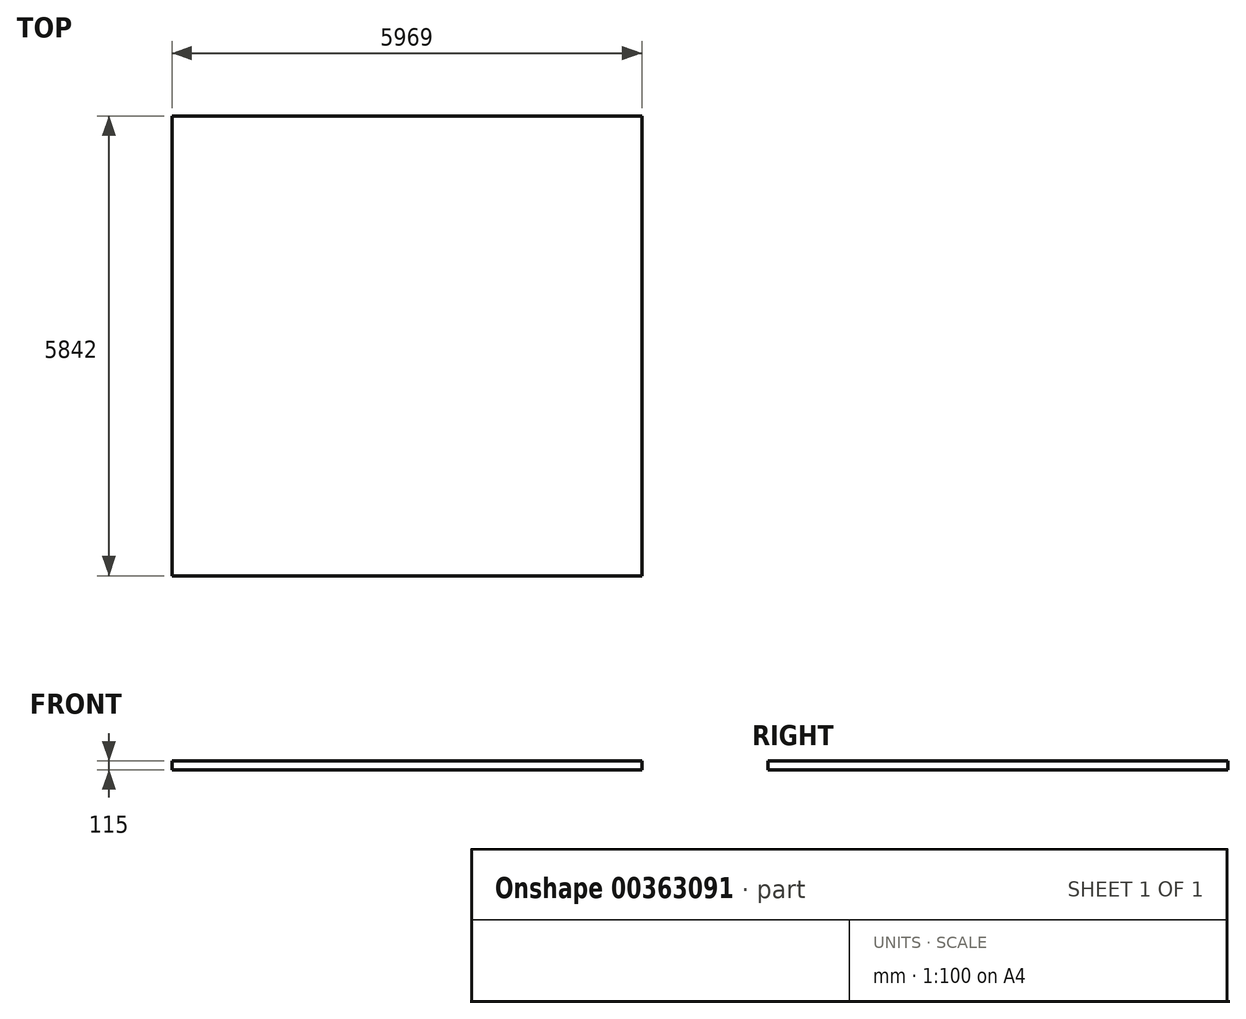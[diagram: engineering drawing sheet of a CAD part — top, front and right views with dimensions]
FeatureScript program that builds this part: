
annotation { "Feature Type Name" : "Feature", "Feature Type Description" : "" }
export const myFeature = defineFeature(function(context is Context, id is Id, definition is map)
    precondition{}
    {
        {
            assignVariable(context, id + "F0", {"name" : "hgt", "anyValue" : 115});
        }
        {
            var Q0;
            Q0=qCreatedBy(makeId("Top.planeOp"),FACE);
            var sketch = newSketch(context, id + "F1", { "sketchPlane" : qUnion([Q0])});
            skLineSegment(sketch, "E0.bottom", {"start": v(2984.5, 2921) * mm, "end": v(-2984.5, 2921) * mm});
            skLineSegment(sketch, "E0.top", {"start": v(2984.5, -2921) * mm, "end": v(-2984.5, -2921) * mm});
            skLineSegment(sketch, "E0.left", {"start": v(2984.5, 2921) * mm, "end": v(2984.5, -2921) * mm});
            skLineSegment(sketch, "E0.right", {"start": v(-2984.5, 2921) * mm, "end": v(-2984.5, -2921) * mm});
            skPoint(sketch, "E0.middle", {"position": v(0, 0) * mm});
            skSolve(sketch);
        }
        {
            var Q0;
            Q0 = qSketchRegion(id + "F1", true);
            extrude(context, id + "F2", {"entities" : qUnion([Q0]), "depth" : (getVariable(context, 'hgt')) * mm});
        }
    });
